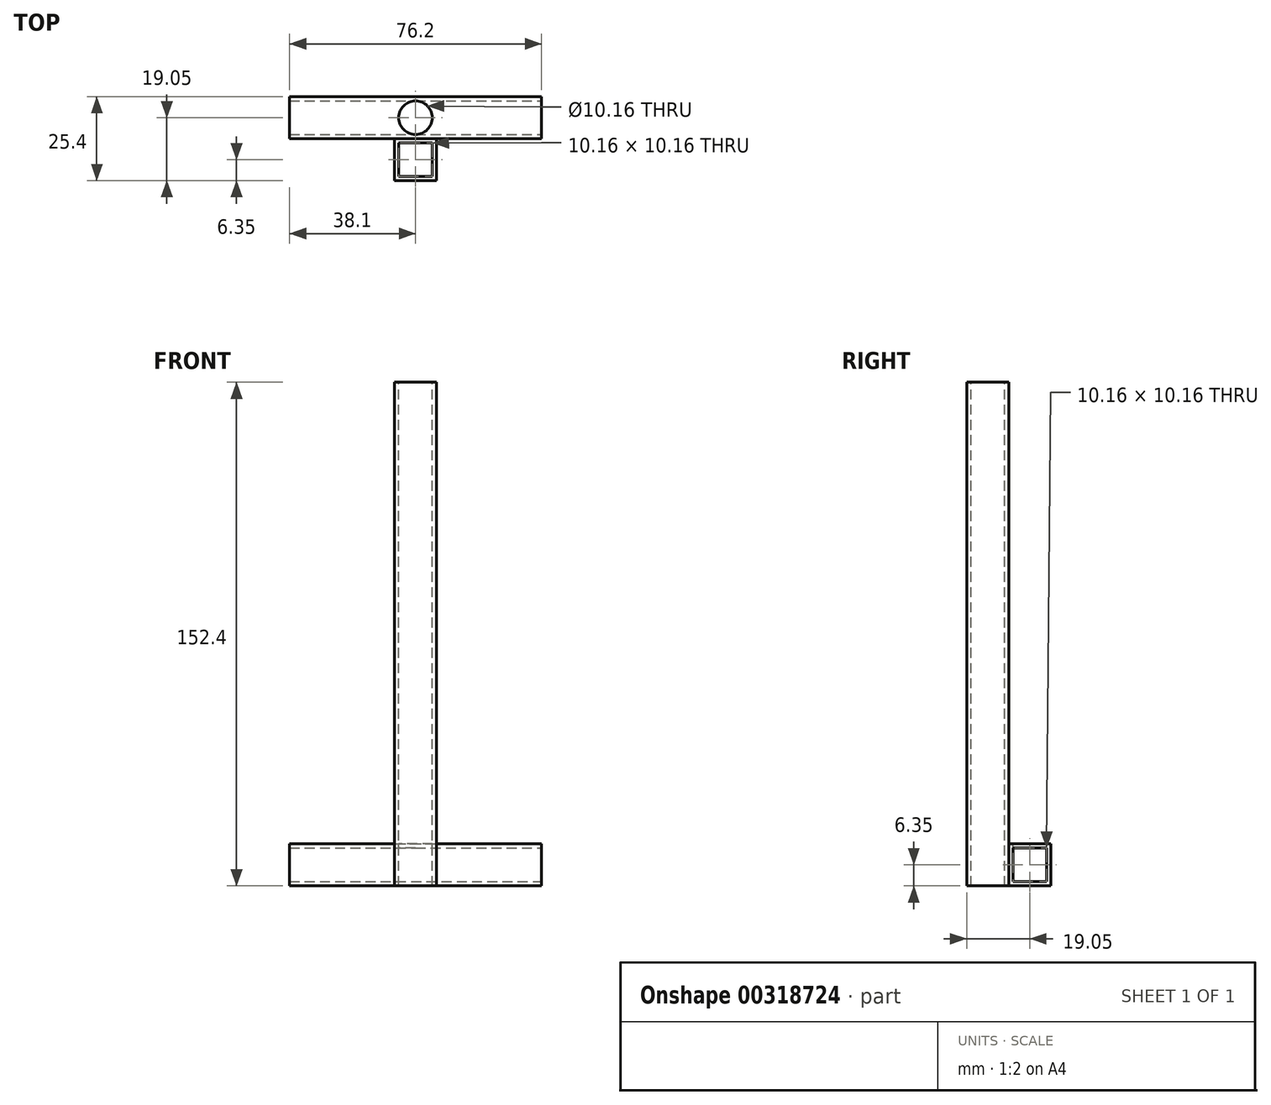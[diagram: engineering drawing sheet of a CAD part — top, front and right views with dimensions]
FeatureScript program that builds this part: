
annotation { "Feature Type Name" : "Feature", "Feature Type Description" : "" }
export const myFeature = defineFeature(function(context is Context, id is Id, definition is map)
    precondition{}
    {
        {
            var Q0;
            Q0=qCreatedBy(makeId("Top.planeOp"),FACE);
            var sketch = newSketch(context, id + "F0", { "sketchPlane" : qUnion([Q0])});
            skLineSegment(sketch, "E0.bottom", {"start": v(0, 0) * mm, "end": v(76.2, 0) * mm});
            skLineSegment(sketch, "E0.top", {"start": v(0, 12.7) * mm, "end": v(76.2, 12.7) * mm});
            skLineSegment(sketch, "E0.left", {"start": v(0, 0) * mm, "end": v(0, 12.7) * mm});
            skLineSegment(sketch, "E0.right", {"start": v(76.2, 0) * mm, "end": v(76.2, 12.7) * mm});
            skSolve(sketch);
        }
        {
            var Q0;
            Q0 = qSketchRegion(id + "F0", true);
            extrude(context, id + "F1", {"entities" : qUnion([Q0]), "depth" : 12.7 * mm});
        }
        {
            var Q0;
            Q0=makeQuery(id+"F1.opExtrude","SWEPT_FACE",FACE,{"disambiguationData":[OSD([sQuery(id+"F0.wireOp",EDGE,"E0.right")])]});
            var sketch = newSketch(context, id + "F2", { "sketchPlane" : qUnion([Q0])});
            skLineSegment(sketch, "E1.0", {"start": v(1.27, 11.43) * mm, "end": v(11.43, 11.43) * mm});
            skLineSegment(sketch, "E2.0", {"start": v(1.27, 11.43) * mm, "end": v(1.27, 1.27) * mm});
            skLineSegment(sketch, "E3.0", {"start": v(1.27, 1.27) * mm, "end": v(11.43, 1.27) * mm});
            skLineSegment(sketch, "E4.0", {"start": v(11.43, 11.43) * mm, "end": v(11.43, 1.27) * mm});
            skSolve(sketch);
        }
        {
            var Q0;
            Q0 = qSketchRegion(id + "F2", true);
            extrude(context, id + "F3", {"entities" : qUnion([Q0]), "operationType" : NewBodyOperationType.REMOVE, "endBound" : BoundingType.THROUGH_ALL, "oppositeDirection" : true, "depth" : 25.4 * mm});
        }
        {
            var Q0;
            Q0=makeQuery(id+"F1.opExtrude","CAP_FACE",FACE,{"disambiguationData":[OSD([sQuery(id+"F0.wireOp",EDGE,"E0.bottom"),sQuery(id+"F0.wireOp",EDGE,"E0.top"),sQuery(id+"F0.wireOp",EDGE,"E0.left"),sQuery(id+"F0.wireOp",EDGE,"E0.right")])],"isStart":false});
            var sketch = newSketch(context, id + "F4", { "sketchPlane" : qUnion([Q0])});
            skCircle(sketch, "E5", {"center": v(38.1, 6.35) * mm, "radius": 5.08 * mm});
            skPoint(sketch, "E5.centerSnap0", {"position": v(38.1, 0) * mm});
            skSolve(sketch);
        }
        {
            var Q0;
            Q0 = qSketchRegion(id + "F4", true);
            extrude(context, id + "F5", {"entities" : qUnion([Q0]), "operationType" : NewBodyOperationType.REMOVE, "endBound" : BoundingType.UP_TO_NEXT, "oppositeDirection" : true, "depth" : 25.4 * mm});
        }
        {
            var Q0;
            Q0=makeQuery(id+"F1.opExtrude","SWEPT_FACE",FACE,{"disambiguationData":[OSD([sQuery(id+"F0.wireOp",EDGE,"E0.bottom")])]});
            var sketch = newSketch(context, id + "F6", { "sketchPlane" : qUnion([Q0])});
            skLineSegment(sketch, "E6", {"start": v(31.75, 0) * mm, "end": v(44.45, 0) * mm});
            skLineSegment(sketch, "E7", {"start": v(31.75, 0) * mm, "end": v(31.75, 152.4) * mm});
            skLineSegment(sketch, "E8", {"start": v(31.75, 152.4) * mm, "end": v(44.45, 152.4) * mm});
            skLineSegment(sketch, "E9", {"start": v(44.45, 152.4) * mm, "end": v(44.45, 0) * mm});
            skLineSegment(sketch, "E10", {"start": v(38.1, 12.7) * mm, "end": v(38.1, 0) * mm, "construction": true});
            skSolve(sketch);
        }
        {
            var Q0;
            Q0 = qSketchRegion(id + "F6", true);
            extrude(context, id + "F7", {"entities" : qUnion([Q0]), "operationType" : NewBodyOperationType.ADD, "depth" : 12.7 * mm});
        }
        {
            var Q0;
            Q0=makeQuery(id+"F7.opExtrude","SWEPT_FACE",FACE,{"disambiguationData":[OSD([sQuery(id+"F6.wireOp",EDGE,"E8")])]});
            var sketch = newSketch(context, id + "F8", { "sketchPlane" : qUnion([Q0])});
            skLineSegment(sketch, "E11.bottom", {"start": v(33.02, -1.27) * mm, "end": v(43.18, -1.27) * mm});
            skLineSegment(sketch, "E11.top", {"start": v(33.02, -11.43) * mm, "end": v(43.18, -11.43) * mm});
            skLineSegment(sketch, "E11.left", {"start": v(33.02, -1.27) * mm, "end": v(33.02, -11.43) * mm});
            skLineSegment(sketch, "E11.right", {"start": v(43.18, -1.27) * mm, "end": v(43.18, -11.43) * mm});
            skSolve(sketch);
        }
        {
            var Q0;
            Q0=makeQuery(id+"F8.imprint","IMPRINT",FACE,{"disambiguationData":[TD([[makeQuery(id+"F8.imprint","IMPRINT",EDGE,{"derivedFrom":sQuery(id+"F8.wireOp",EDGE,"E11.bottom")}),-1.0]])]});
            extrude(context, id + "F9", {"entities" : qUnion([Q0]), "operationType" : NewBodyOperationType.REMOVE, "endBound" : BoundingType.THROUGH_ALL, "oppositeDirection" : true, "depth" : 25.4 * mm});
        }
    });
